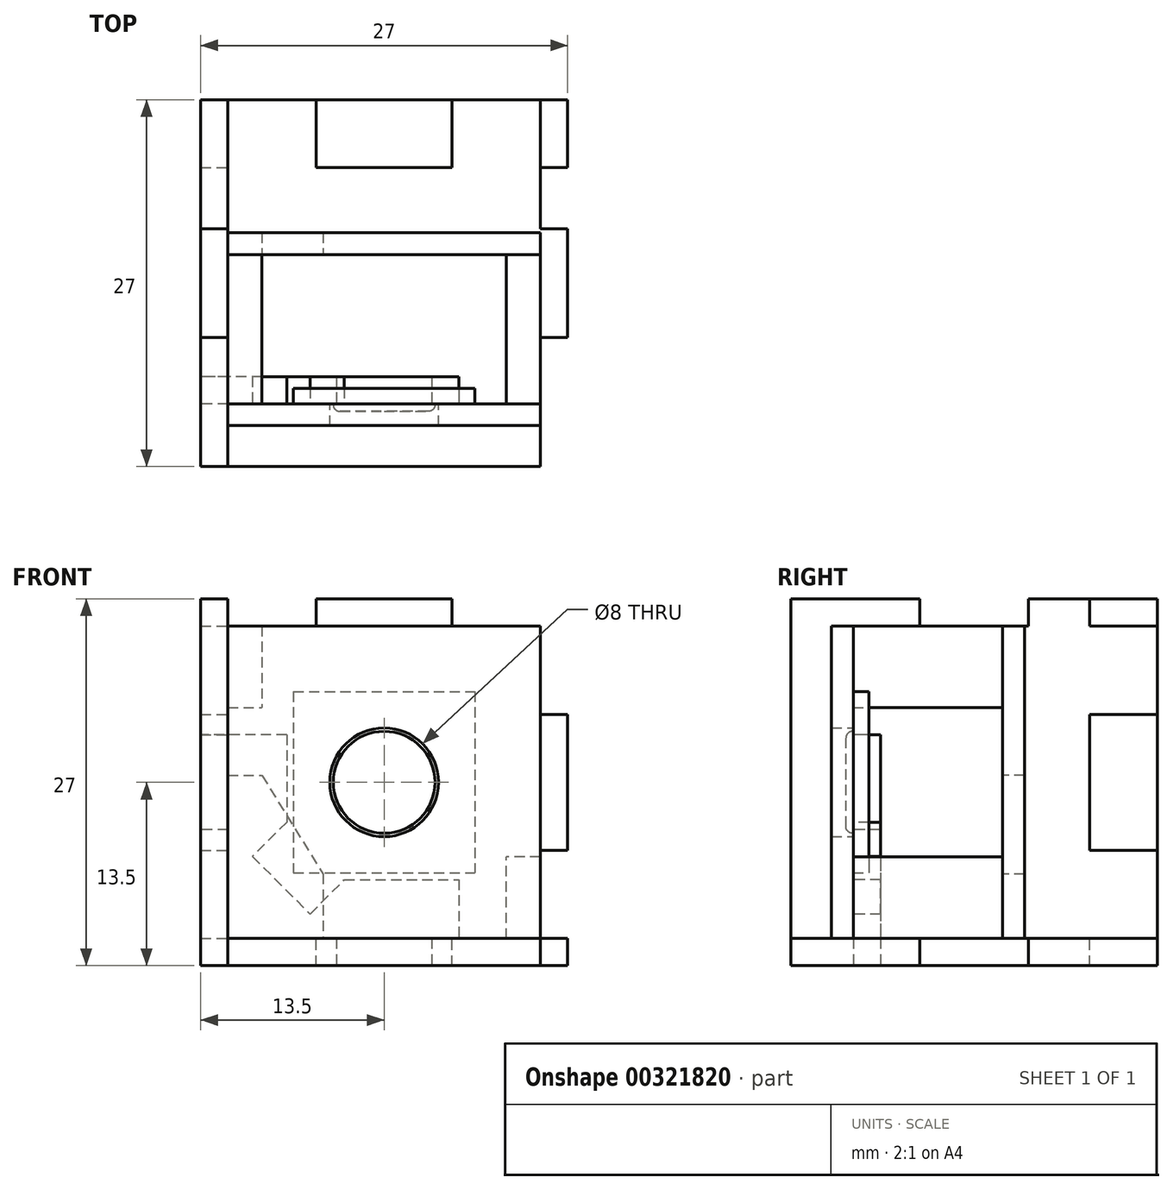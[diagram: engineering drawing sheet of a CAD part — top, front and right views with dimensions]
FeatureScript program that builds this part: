
annotation { "Feature Type Name" : "Feature", "Feature Type Description" : "" }
export const myFeature = defineFeature(function(context is Context, id is Id, definition is map)
    precondition{}
    {
        {
            var Q0;
            Q0=qCreatedBy(makeId("Front.planeOp"),FACE);
            var sketch = newSketch(context, id + "F0", { "sketchPlane" : qUnion([Q0])});
            skLineSegment(sketch, "E0.bottom", {"start": v(-6.68, 6.68) * mm, "end": v(6.68, 6.68) * mm});
            skLineSegment(sketch, "E0.top", {"start": v(-6.68, -6.68) * mm, "end": v(6.68, -6.68) * mm});
            skLineSegment(sketch, "E0.left", {"start": v(-6.68, 6.68) * mm, "end": v(-6.68, -6.68) * mm});
            skLineSegment(sketch, "E0.right", {"start": v(6.68, 6.68) * mm, "end": v(6.67, -6.68) * mm});
            skPoint(sketch, "E0.middle", {"position": v(0, 0) * mm});
            skSolve(sketch);
        }
        {
            var Q0;
            Q0 = qSketchRegion(id + "F0", true);
            extrude(context, id + "F1", {"entities" : qUnion([Q0]), "depth" : 1.15 * mm});
        }
        {
            var Q0;
            Q0=makeQuery(id+"F1.opExtrude","CAP_FACE",FACE,{"disambiguationData":[OSD([sQuery(id+"F0.wireOp",EDGE,"E0.bottom"),sQuery(id+"F0.wireOp",EDGE,"E0.top"),sQuery(id+"F0.wireOp",EDGE,"E0.left"),sQuery(id+"F0.wireOp",EDGE,"E0.right")])],"isStart":false});
            var sketch = newSketch(context, id + "F2", { "sketchPlane" : qUnion([Q0])});
            skCircle(sketch, "E1", {"center": v(0, 0) * mm, "radius": 3.75 * mm});
            skSolve(sketch);
        }
        {
            var Q0;
            Q0 = qSketchRegion(id + "F2", true);
            extrude(context, id + "F3", {"entities" : qUnion([Q0]), "operationType" : NewBodyOperationType.ADD, "depth" : 0.55 * mm});
        }
        {
            var Q0;
            Q0=makeQuery(id+"F3.opExtrude","CAP_FACE",FACE,{"disambiguationData":[OSD([sQuery(id+"F2.wireOp",EDGE,"E1")])],"isStart":false});
            fillet(context, id + "F4", {"entities" : qUnion([Q0]), "radius" : 0.5 * mm, "tangentPropagation" : true, "allowEdgeOverflow" : false});
        }
        {
            var Q0;
            Q0=makeQuery(id+"F1.opExtrude","CAP_FACE",FACE,{"disambiguationData":[OSD([sQuery(id+"F0.wireOp",EDGE,"E0.bottom"),sQuery(id+"F0.wireOp",EDGE,"E0.top"),sQuery(id+"F0.wireOp",EDGE,"E0.left"),sQuery(id+"F0.wireOp",EDGE,"E0.right")])],"isStart":false});
            var sketch = newSketch(context, id + "F5", { "sketchPlane" : qUnion([Q0])});
            skLineSegment(sketch, "E2.bottom", {"start": v(-11.5, 11.5) * mm, "end": v(11.5, 11.5) * mm});
            skLineSegment(sketch, "E2.top", {"start": v(-11.5, -11.5) * mm, "end": v(11.5, -11.5) * mm});
            skLineSegment(sketch, "E2.left", {"start": v(-11.5, 11.5) * mm, "end": v(-11.5, -11.5) * mm});
            skLineSegment(sketch, "E2.right", {"start": v(11.5, 11.5) * mm, "end": v(11.5, -11.5) * mm});
            skPoint(sketch, "E2.middle", {"position": v(0, 0) * mm});
            skCircle(sketch, "E3", {"center": v(0, 0) * mm, "radius": 4 * mm});
            skSolve(sketch);
        }
        {
            var Q0;
            Q0 = qSketchRegion(id + "F5", true);
            extrude(context, id + "F6", {"entities" : qUnion([Q0]), "depth" : 1.6 * mm});
        }
        {
            var Q0;
            Q0=makeQuery(id+"F6.opExtrude","CAP_FACE",FACE,{"disambiguationData":[OSD([sQuery(id+"F5.wireOp",EDGE,"E2.bottom"),sQuery(id+"F5.wireOp",EDGE,"E2.top"),sQuery(id+"F5.wireOp",EDGE,"E2.left"),sQuery(id+"F5.wireOp",EDGE,"E2.right"),sQuery(id+"F5.wireOp",EDGE,"E3")])],"isStart":true});
            cPlane(context, id + "F7", {"entities" : qUnion([Q0]), "cplaneType" : CPlaneType.OFFSET, "offset" : 11 * mm, "width" : 150 * mm, "height" : 150 * mm});
        }
        {
            var Q0;
            Q0=qCreatedBy(id+"F7.planeOp",FACE);
            var sketch = newSketch(context, id + "F8", { "sketchPlane" : qUnion([Q0])});
            skLineSegment(sketch, "E4.bottom", {"start": v(11.5, 11.5) * mm, "end": v(-11.5, 11.5) * mm});
            skLineSegment(sketch, "E4.top", {"start": v(11.5, -11.5) * mm, "end": v(-11.5, -11.5) * mm});
            skLineSegment(sketch, "E4.left", {"start": v(11.5, 11.5) * mm, "end": v(11.5, -11.5) * mm});
            skLineSegment(sketch, "E4.right", {"start": v(-11.5, 11.5) * mm, "end": v(-11.5, -11.5) * mm});
            skPoint(sketch, "E4.middle", {"position": v(0, 0) * mm});
            skLineSegment(sketch, "E5", {"start": v(11.5, 0.5) * mm, "end": v(9, 0.5) * mm});
            skLineSegment(sketch, "E6", {"start": v(9, 0.5) * mm, "end": v(4.5, -6.75) * mm});
            skLineSegment(sketch, "E7", {"start": v(4.5, -6.75) * mm, "end": v(4.5, -11.5) * mm});
            skSolve(sketch);
        }
        {
            var Q0;
            {var subQ1=sQuery(id+"F8.wireOp",EDGE,"E4.bottom");Q0=makeQuery(id+"F8.imprint","IMPRINT",FACE,{"disambiguationData":[TD([[makeQuery(id+"F8.imprint","IMPRINT",EDGE,{"derivedFrom":subQ1}),1.0]])]});}
            extrude(context, id + "F9", {"entities" : qUnion([Q0]), "depth" : 1.6 * mm});
        }
        {
            var Q0;
            Q0=makeQuery(id+"F9.opExtrude","CAP_FACE",FACE,{"disambiguationData":[OSD([sQuery(id+"F8.wireOp",EDGE,"E4.bottom"),sQuery(id+"F8.wireOp",EDGE,"E4.top"),sQuery(id+"F8.wireOp",EDGE,"E4.left"),sQuery(id+"F8.wireOp",EDGE,"E4.right"),sQuery(id+"F8.wireOp",EDGE,"E5"),sQuery(id+"F8.wireOp",EDGE,"E6"),sQuery(id+"F8.wireOp",EDGE,"E7")])],"isStart":true});
            var sketch = newSketch(context, id + "F10", { "sketchPlane" : qUnion([Q0])});
            skLineSegment(sketch, "E8.bottom", {"start": v(-11.5, 11.5) * mm, "end": v(-9, 11.5) * mm});
            skLineSegment(sketch, "E8.top", {"start": v(-11.5, 5.5) * mm, "end": v(-9, 5.5) * mm});
            skLineSegment(sketch, "E8.left", {"start": v(-11.5, 11.5) * mm, "end": v(-11.5, 5.5) * mm});
            skLineSegment(sketch, "E8.right", {"start": v(-9, 11.5) * mm, "end": v(-9, 5.5) * mm});
            skLineSegment(sketch, "E9.bottom", {"start": v(11.5, -11.5) * mm, "end": v(9, -11.5) * mm});
            skLineSegment(sketch, "E9.top", {"start": v(11.5, -5.5) * mm, "end": v(9, -5.5) * mm});
            skLineSegment(sketch, "E9.left", {"start": v(11.5, -11.5) * mm, "end": v(11.5, -5.5) * mm});
            skLineSegment(sketch, "E9.right", {"start": v(9, -11.5) * mm, "end": v(9, -5.5) * mm});
            skSolve(sketch);
        }
        {
            var Q0;
            Q0 = qSketchRegion(id + "F10", true);
            extrude(context, id + "F11", {"entities" : qUnion([Q0]), "endBound" : BoundingType.UP_TO_NEXT, "depth" : 25 * mm});
        }
        {
            var Q0;
            Q0=makeQuery(id+"F6.opExtrude","CAP_FACE",FACE,{"disambiguationData":[OSD([sQuery(id+"F5.wireOp",EDGE,"E2.bottom"),sQuery(id+"F5.wireOp",EDGE,"E2.top"),sQuery(id+"F5.wireOp",EDGE,"E2.left"),sQuery(id+"F5.wireOp",EDGE,"E2.right"),sQuery(id+"F5.wireOp",EDGE,"E3")])],"isStart":true});
            var sketch = newSketch(context, id + "F12", { "sketchPlane" : qUnion([Q0])});
            skPoint(sketch, "E10.middle", {"position": v(0, 0) * mm});
            skLineSegment(sketch, "E11.bottom", {"start": v(5.46, -9) * mm, "end": v(9, -5.45) * mm, "construction": true});
            skLineSegment(sketch, "E11.top", {"start": v(1.92, -5.46) * mm, "end": v(5.46, -1.92) * mm, "construction": true});
            skLineSegment(sketch, "E11.left", {"start": v(5.46, -9) * mm, "end": v(1.92, -5.46) * mm, "construction": true});
            skLineSegment(sketch, "E11.right", {"start": v(9, -5.46) * mm, "end": v(5.46, -1.92) * mm, "construction": true});
            skPoint(sketch, "E11.middle", {"position": v(5.46, -5.46) * mm});
            skLineSegment(sketch, "E12", {"start": v(5.46, -5.46) * mm, "end": v(5.46, -1.92) * mm, "construction": true});
            skLineSegment(sketch, "E13.bottom", {"start": v(11.5, -3.5) * mm, "end": v(13.5, -3.5) * mm});
            skLineSegment(sketch, "E13.top", {"start": v(11.5, 3.5) * mm, "end": v(13.5, 3.5) * mm});
            skLineSegment(sketch, "E13.left", {"start": v(11.5, -3.5) * mm, "end": v(11.5, 3.5) * mm});
            skLineSegment(sketch, "E13.right", {"start": v(13.5, -3.5) * mm, "end": v(13.5, 3.5) * mm});
            skPoint(sketch, "E13.middle", {"position": v(12.5, 0) * mm});
            skLineSegment(sketch, "E14.bottom", {"start": v(3.5, -11.5) * mm, "end": v(-3.5, -11.5) * mm});
            skLineSegment(sketch, "E14.top", {"start": v(3.5, -13.5) * mm, "end": v(-3.5, -13.5) * mm});
            skLineSegment(sketch, "E14.left", {"start": v(3.5, -11.5) * mm, "end": v(3.5, -13.5) * mm});
            skLineSegment(sketch, "E14.right", {"start": v(-3.5, -11.5) * mm, "end": v(-3.5, -13.5) * mm});
            skPoint(sketch, "E14.middle", {"position": v(0, -12.5) * mm});
            skLineSegment(sketch, "E15", {"start": v(11.5, -3.5) * mm, "end": v(11.5, -11.5) * mm});
            skLineSegment(sketch, "E16", {"start": v(11.5, -11.5) * mm, "end": v(3.5, -11.5) * mm});
            skLineSegment(sketch, "E17", {"start": v(11.5, 3.5) * mm, "end": v(7.17, 3.5) * mm});
            skLineSegment(sketch, "E18", {"start": v(7.17, 3.5) * mm, "end": v(7.18, -2.93) * mm});
            skLineSegment(sketch, "E19", {"start": v(7.18, -2.93) * mm, "end": v(9.7, -5.46) * mm});
            skLineSegment(sketch, "E20", {"start": v(9.7, -5.46) * mm, "end": v(5.46, -9.7) * mm});
            skLineSegment(sketch, "E21", {"start": v(5.46, -9.7) * mm, "end": v(2.93, -7.18) * mm});
            skLineSegment(sketch, "E22", {"start": v(2.93, -7.18) * mm, "end": v(-5.5, -7.18) * mm});
            skLineSegment(sketch, "E23", {"start": v(-5.5, -7.18) * mm, "end": v(-5.5, -11.5) * mm});
            skLineSegment(sketch, "E24", {"start": v(-5.5, -11.5) * mm, "end": v(-3.5, -11.5) * mm});
            skLineSegment(sketch, "E25", {"start": v(7.58, -7.58) * mm, "end": v(0, 0) * mm, "construction": true});
            skSolve(sketch);
        }
        {
            var Q0;
            Q0 = qSketchRegion(id + "F12", true);
            extrude(context, id + "F13", {"entities" : qUnion([Q0]), "depth" : 2 * mm});
        }
        {
            var Q0;
            Q0=makeQuery(id+"F13.opExtrude","SWEPT_FACE",FACE,{"disambiguationData":[OSD([sQuery(id+"F12.wireOp",EDGE,"E16")])]});
            var sketch = newSketch(context, id + "F14", { "sketchPlane" : qUnion([Q0])});
            skLineSegment(sketch, "E26.bottom", {"start": v(-11.5, 5.75) * mm, "end": v(11.5, 5.75) * mm});
            skLineSegment(sketch, "E26.top", {"start": v(-11.5, -21.25) * mm, "end": v(11.5, -21.25) * mm});
            skLineSegment(sketch, "E26.left", {"start": v(-11.5, 5.75) * mm, "end": v(-11.5, -21.25) * mm});
            skLineSegment(sketch, "E26.right", {"start": v(11.5, 5.75) * mm, "end": v(11.5, -21.25) * mm});
            skPoint(sketch, "E26.middle", {"position": v(0, -7.75) * mm});
            skLineSegment(sketch, "E27.0", {"start": v(-3.5, 1.15) * mm, "end": v(3.5, 1.15) * mm});
            skLineSegment(sketch, "E27.1", {"start": v(-3.5, -0.85) * mm, "end": v(-3.5, 1.15) * mm});
            skLineSegment(sketch, "E27.2", {"start": v(-3.5, -0.85) * mm, "end": v(3.5, -0.85) * mm});
            skLineSegment(sketch, "E27.3", {"start": v(3.5, -0.85) * mm, "end": v(3.5, 1.15) * mm});
            skLineSegment(sketch, "E28.bottom", {"start": v(5, -21.25) * mm, "end": v(-5, -21.25) * mm});
            skLineSegment(sketch, "E28.top", {"start": v(5, -16.25) * mm, "end": v(-5, -16.25) * mm});
            skLineSegment(sketch, "E28.left", {"start": v(5, -21.25) * mm, "end": v(5, -16.25) * mm});
            skLineSegment(sketch, "E28.right", {"start": v(-5, -21.25) * mm, "end": v(-5, -16.25) * mm});
            skPoint(sketch, "E28.middle", {"position": v(0, -18.75) * mm});
            skLineSegment(sketch, "E29.bottom", {"start": v(-11.5, -3.75) * mm, "end": v(-13.5, -3.75) * mm});
            skLineSegment(sketch, "E29.top", {"start": v(-11.5, -11.75) * mm, "end": v(-13.5, -11.75) * mm});
            skLineSegment(sketch, "E29.left", {"start": v(-11.5, -3.75) * mm, "end": v(-11.5, -11.75) * mm});
            skLineSegment(sketch, "E29.right", {"start": v(-13.5, -3.75) * mm, "end": v(-13.5, -11.75) * mm});
            skPoint(sketch, "E29.middle", {"position": v(-12.5, -7.75) * mm});
            skLineSegment(sketch, "E30", {"start": v(0, -7.75) * mm, "end": v(0, -3.1) * mm, "construction": true});
            skLineSegment(sketch, "E31.MirrorCS", {"start": v(11.5, -3.75) * mm, "end": v(13.5, -3.75) * mm});
            skLineSegment(sketch, "E32.MirrorCS", {"start": v(13.5, -3.75) * mm, "end": v(13.5, -11.75) * mm});
            skLineSegment(sketch, "E33.MirrorCS", {"start": v(11.5, -11.75) * mm, "end": v(13.5, -11.75) * mm});
            skSolve(sketch);
        }
        {
            var Q0;
            Q0=makeQuery(id+"F14.imprint","IMPRINT",FACE,{"disambiguationData":[TD([[makeQuery(id+"F14.imprint","IMPRINT",EDGE,{"derivedFrom":sQuery(id+"F14.wireOp",EDGE,"E27.1")}),1.0]])]});
            var Q1;
            {var subQ6=sQuery(id+"F14.wireOp",EDGE,"E26.bottom");Q1=makeQuery(id+"F14.imprint","IMPRINT",FACE,{"disambiguationData":[TD([[makeQuery(id+"F14.imprint","IMPRINT",EDGE,{"derivedFrom":subQ6}),-1.0]])]});}
            var Q2;
            Q2=makeQuery(id+"F14.imprint","IMPRINT",FACE,{"disambiguationData":[TD([[makeQuery(id+"F14.imprint","IMPRINT",EDGE,{"derivedFrom":sQuery(id+"F14.wireOp",EDGE,"E29.bottom")}),1.0]])]});
            var Q3;
            {var subQ0=sQuery(id+"F14.wireOp",EDGE,"E31.MirrorCS");Q3=makeQuery(id+"F14.imprint","IMPRINT",FACE,{"disambiguationData":[TD([[makeQuery(id+"F14.imprint","IMPRINT",EDGE,{"derivedFrom":subQ0}),-1.0]])]});}
            extrude(context, id + "F15", {"entities" : qUnion([Q0, Q1, Q2, Q3]), "depth" : 2 * mm});
        }
        {
            var Q0;
            Q0=makeQuery(id+"F13.opExtrude","SWEPT_FACE",FACE,{"disambiguationData":[OSD([sQuery(id+"F12.wireOp",EDGE,"E15")])]});
            var sketch = newSketch(context, id + "F16", { "sketchPlane" : qUnion([Q0])});
            skLineSegment(sketch, "E34.bottom", {"start": v(5.75, -13.5) * mm, "end": v(-21.25, -13.5) * mm});
            skLineSegment(sketch, "E34.top", {"start": v(5.75, 13.5) * mm, "end": v(-21.25, 13.5) * mm});
            skLineSegment(sketch, "E34.left", {"start": v(5.75, -13.5) * mm, "end": v(5.75, 13.5) * mm});
            skLineSegment(sketch, "E34.right", {"start": v(-21.25, -13.5) * mm, "end": v(-21.25, 13.5) * mm});
            skPoint(sketch, "E34.middle", {"position": v(-7.75, 0) * mm});
            skLineSegment(sketch, "E35.0", {"start": v(1.15, -3.5) * mm, "end": v(1.15, 3.5) * mm});
            skLineSegment(sketch, "E35.1", {"start": v(-0.85, 3.5) * mm, "end": v(1.15, 3.5) * mm});
            skLineSegment(sketch, "E35.2", {"start": v(-0.85, -3.5) * mm, "end": v(-0.85, 3.5) * mm});
            skLineSegment(sketch, "E35.3", {"start": v(-0.85, -3.5) * mm, "end": v(1.15, -3.5) * mm});
            skLineSegment(sketch, "E36.bottom", {"start": v(-21.25, -5) * mm, "end": v(-16.25, -5) * mm});
            skLineSegment(sketch, "E36.top", {"start": v(-21.25, 5) * mm, "end": v(-16.25, 5) * mm});
            skLineSegment(sketch, "E36.left", {"start": v(-21.25, -5) * mm, "end": v(-21.25, 5) * mm});
            skLineSegment(sketch, "E36.right", {"start": v(-16.25, -5) * mm, "end": v(-16.25, 5) * mm});
            skPoint(sketch, "E36.middle", {"position": v(-18.75, 0) * mm});
            skLineSegment(sketch, "E37.0", {"start": v(-11.75, -13.5) * mm, "end": v(-11.75, -11.5) * mm});
            skLineSegment(sketch, "E37.1", {"start": v(-3.75, -11.5) * mm, "end": v(-11.75, -11.5) * mm});
            skLineSegment(sketch, "E37.2", {"start": v(-3.75, -13.5) * mm, "end": v(-3.75, -11.5) * mm});
            skLineSegment(sketch, "E38", {"start": v(-7.75, 0) * mm, "end": v(-2.75, 0) * mm, "construction": true});
            skLineSegment(sketch, "E39.MirrorCS", {"start": v(-3.75, 13.5) * mm, "end": v(-3.75, 11.5) * mm});
            skLineSegment(sketch, "E40.MirrorCS", {"start": v(-3.75, 11.5) * mm, "end": v(-11.75, 11.5) * mm});
            skLineSegment(sketch, "E41.MirrorCS", {"start": v(-11.75, 13.5) * mm, "end": v(-11.75, 11.5) * mm});
            skSolve(sketch);
        }
        {
            var Q0;
            Q0=makeQuery(id+"F16.imprint","IMPRINT",FACE,{"disambiguationData":[TD([[makeQuery(id+"F16.imprint","IMPRINT",EDGE,{"derivedFrom":sQuery(id+"F16.wireOp",EDGE,"E35.3")}),-1.0]])]});
            var Q1;
            {var subQ5=sQuery(id+"F16.wireOp",EDGE,"E34.bottom");Q1=makeQuery(id+"F16.imprint","IMPRINT",FACE,{"disambiguationData":[TD([[makeQuery(id+"F16.imprint","IMPRINT",EDGE,{"derivedFrom":subQ5}),-1.0]])]});}
            extrude(context, id + "F17", {"entities" : qUnion([Q0, Q1]), "depth" : 2 * mm});
        }
        {
            var Q0;
            Q0=makeQuery(id+"F15.opExtrude","SWEPT_FACE",FACE,{"disambiguationData":[OSD([sQuery(id+"F14.wireOp",EDGE,"E28.top")])]});
            var sketch = newSketch(context, id + "F18", { "sketchPlane" : qUnion([Q0])});
            skLineSegment(sketch, "E42.bottom", {"start": v(-11.5, 11.5) * mm, "end": v(11.5, 11.5) * mm});
            skLineSegment(sketch, "E42.top", {"start": v(-11.5, -11.5) * mm, "end": v(11.5, -11.5) * mm});
            skLineSegment(sketch, "E42.left", {"start": v(-11.5, 11.5) * mm, "end": v(-11.5, -11.5) * mm});
            skLineSegment(sketch, "E42.right", {"start": v(11.5, 11.5) * mm, "end": v(11.5, -11.5) * mm});
            skPoint(sketch, "E42.middle", {"position": v(0, 0) * mm});
            skLineSegment(sketch, "E43.bottom", {"start": v(-5, -13.5) * mm, "end": v(5, -13.5) * mm});
            skLineSegment(sketch, "E43.top", {"start": v(-5, -11.5) * mm, "end": v(5, -11.5) * mm});
            skLineSegment(sketch, "E43.left", {"start": v(-5, -13.5) * mm, "end": v(-5, -11.5) * mm});
            skLineSegment(sketch, "E43.right", {"start": v(5, -13.5) * mm, "end": v(5, -11.5) * mm});
            skLineSegment(sketch, "E44.1.1", {"start": v(13.5, -5) * mm, "end": v(11.5, -5) * mm});
            skLineSegment(sketch, "E44.1.2", {"start": v(13.5, -5) * mm, "end": v(13.5, 5) * mm});
            skLineSegment(sketch, "E44.1.3", {"start": v(13.5, 5) * mm, "end": v(11.5, 5) * mm});
            skLineSegment(sketch, "E44.2.1", {"start": v(5, 13.5) * mm, "end": v(5, 11.5) * mm});
            skLineSegment(sketch, "E44.2.2", {"start": v(5, 13.5) * mm, "end": v(-5, 13.5) * mm});
            skLineSegment(sketch, "E44.2.3", {"start": v(-5, 13.5) * mm, "end": v(-5, 11.5) * mm});
            skLineSegment(sketch, "E44.3.1", {"start": v(-13.5, 5) * mm, "end": v(-11.5, 5) * mm});
            skLineSegment(sketch, "E44.3.2", {"start": v(-13.5, 5) * mm, "end": v(-13.5, -5) * mm});
            skLineSegment(sketch, "E44.3.3", {"start": v(-13.5, -5) * mm, "end": v(-11.5, -5) * mm});
            skCircle(sketch, "E45", {"center": v(0, 0) * mm, "radius": 2.5 * mm});
            skCircle(sketch, "E46", {"center": v(-7, -7) * mm, "radius": 3 * mm});
            skLineSegment(sketch, "E47", {"start": v(-11.5, -11.5) * mm, "end": v(11.5, 11.5) * mm, "construction": true});
            skCircle(sketch, "E48", {"center": v(7, 7) * mm, "radius": 3 * mm});
            skSolve(sketch);
        }
        {
            var Q0;
            {var subQ11=sQuery(id+"F18.wireOp",EDGE,"E43.top");Q0=makeQuery(id+"F18.imprint","IMPRINT",FACE,{"disambiguationData":[TD([[makeQuery(id+"F18.imprint","IMPRINT",EDGE,{"derivedFrom":subQ11}),1.0]])]});}
            var Q1;
            {var subQ0=sQuery(id+"F18.wireOp",EDGE,"E44.3.1");Q1=makeQuery(id+"F18.imprint","IMPRINT",FACE,{"disambiguationData":[TD([[makeQuery(id+"F18.imprint","IMPRINT",EDGE,{"derivedFrom":subQ0}),-1.0]])]});}
            var Q2;
            Q2=makeQuery(id+"F18.imprint","IMPRINT",FACE,{"disambiguationData":[TD([[makeQuery(id+"F18.imprint","IMPRINT",EDGE,{"derivedFrom":sQuery(id+"F18.wireOp",EDGE,"E43.bottom")}),1.0]])]});
            var Q3;
            {var subQ0=sQuery(id+"F18.wireOp",EDGE,"E44.2.1");Q3=makeQuery(id+"F18.imprint","IMPRINT",FACE,{"disambiguationData":[TD([[makeQuery(id+"F18.imprint","IMPRINT",EDGE,{"derivedFrom":subQ0}),-1.0]])]});}
            var Q4;
            {var subQ0=sQuery(id+"F18.wireOp",EDGE,"E44.1.1");Q4=makeQuery(id+"F18.imprint","IMPRINT",FACE,{"disambiguationData":[TD([[makeQuery(id+"F18.imprint","IMPRINT",EDGE,{"derivedFrom":subQ0}),-1.0]])]});}
            extrude(context, id + "F19", {"entities" : qUnion([Q0, Q1, Q2, Q3, Q4]), "depth" : 5 * mm});
        }
    });
